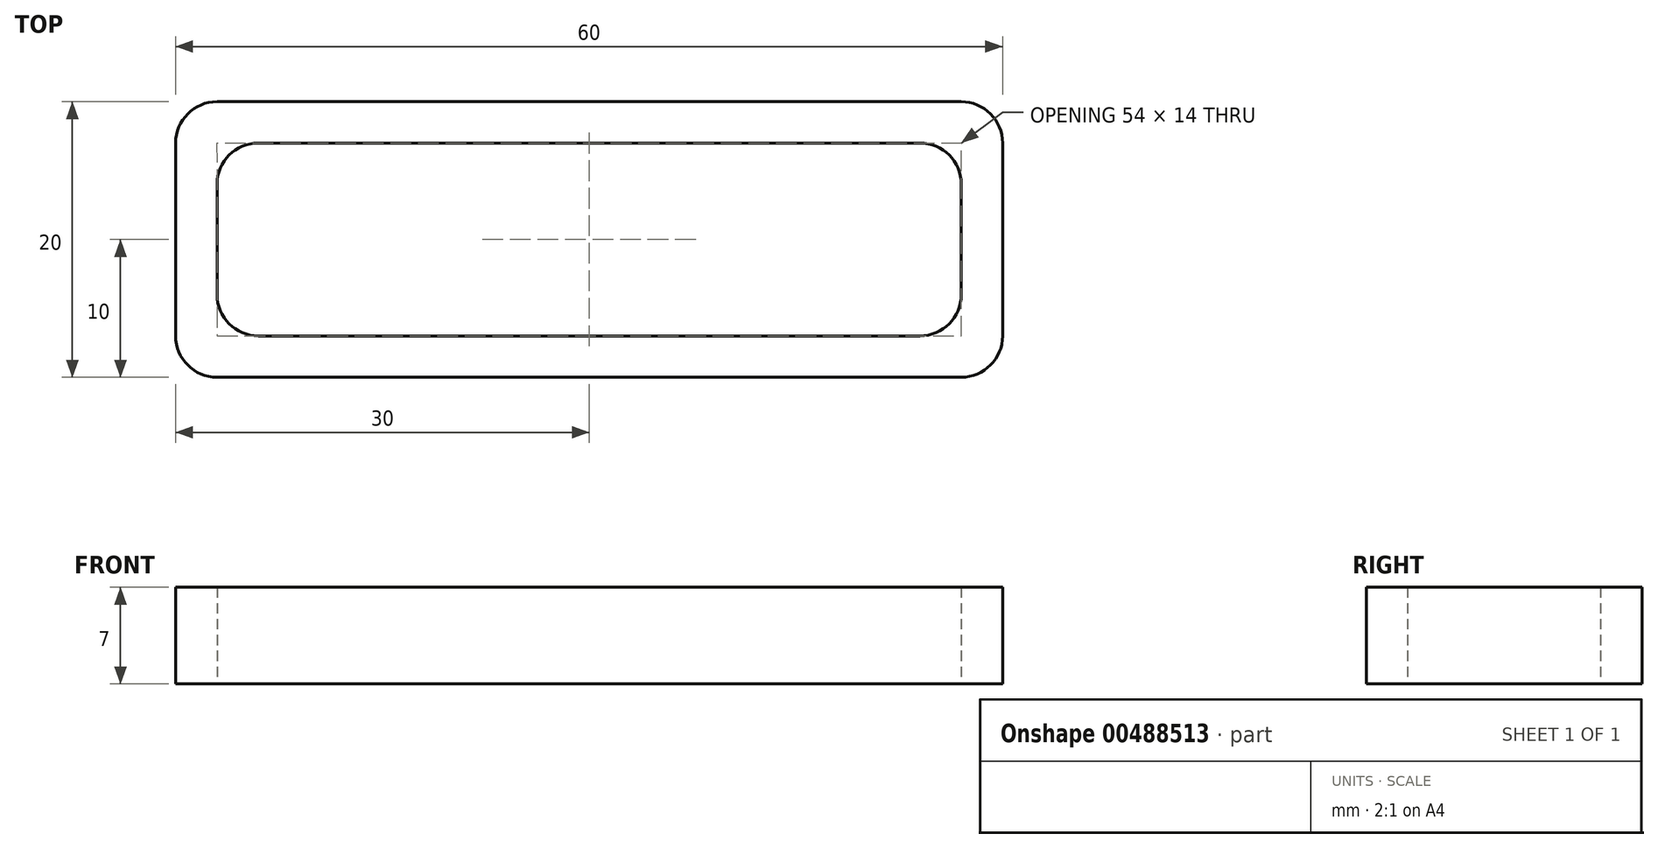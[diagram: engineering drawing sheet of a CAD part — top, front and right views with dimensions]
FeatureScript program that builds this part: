
annotation { "Feature Type Name" : "Feature", "Feature Type Description" : "" }
export const myFeature = defineFeature(function(context is Context, id is Id, definition is map)
    precondition{}
    {
        {
            var Q0;
            Q0=qCreatedBy(makeId("Top.planeOp"),FACE);
            var sketch = newSketch(context, id + "F0", { "sketchPlane" : qUnion([Q0])});
            skLineSegment(sketch, "E0.bottom", {"start": v(30, -10) * mm, "end": v(-30, -10) * mm});
            skLineSegment(sketch, "E0.top", {"start": v(30, 10) * mm, "end": v(-30, 10) * mm});
            skLineSegment(sketch, "E0.left", {"start": v(30, -10) * mm, "end": v(30, 10) * mm});
            skLineSegment(sketch, "E0.right", {"start": v(-30, -10) * mm, "end": v(-30, 10) * mm});
            skPoint(sketch, "E0.middle", {"position": v(0, 0) * mm});
            skLineSegment(sketch, "E1.bottom", {"start": v(-27, 7) * mm, "end": v(27, 7) * mm});
            skLineSegment(sketch, "E1.top", {"start": v(-27, -7) * mm, "end": v(27, -7) * mm});
            skLineSegment(sketch, "E1.left", {"start": v(-27, 7) * mm, "end": v(-27, -7) * mm});
            skLineSegment(sketch, "E1.right", {"start": v(27, 7) * mm, "end": v(27, -7) * mm});
            skSolve(sketch);
        }
        {
            var Q0;
            Q0 = qSketchRegion(id + "F0", true);
            extrude(context, id + "F1", {"entities" : qUnion([Q0]), "endBound" : BoundingType.SYMMETRIC, "depth" : 7 * mm});
        }
        {
            var Q0;
            Q0=makeQuery(id+"F1.opExtrude","SWEPT_EDGE",EDGE,{"disambiguationData":[OSD([sQuery(id+"F0.wireOp",EDGE,"E0.bottom"),sQuery(id+"F0.wireOp",EDGE,"E0.right")])]});
            var Q1;
            Q1=makeQuery(id+"F1.opExtrude","SWEPT_EDGE",EDGE,{"disambiguationData":[OSD([sQuery(id+"F0.wireOp",EDGE,"E0.top"),sQuery(id+"F0.wireOp",EDGE,"E0.right")])]});
            var Q2;
            Q2=makeQuery(id+"F1.opExtrude","SWEPT_EDGE",EDGE,{"disambiguationData":[OSD([sQuery(id+"F0.wireOp",EDGE,"E1.bottom"),sQuery(id+"F0.wireOp",EDGE,"E1.left")])]});
            var Q3;
            Q3=makeQuery(id+"F1.opExtrude","SWEPT_EDGE",EDGE,{"disambiguationData":[OSD([sQuery(id+"F0.wireOp",EDGE,"E1.top"),sQuery(id+"F0.wireOp",EDGE,"E1.left")])]});
            var Q4;
            Q4=makeQuery(id+"F1.opExtrude","SWEPT_EDGE",EDGE,{"disambiguationData":[OSD([sQuery(id+"F0.wireOp",EDGE,"E1.bottom"),sQuery(id+"F0.wireOp",EDGE,"E1.right")])]});
            var Q5;
            Q5=makeQuery(id+"F1.opExtrude","SWEPT_EDGE",EDGE,{"disambiguationData":[OSD([sQuery(id+"F0.wireOp",EDGE,"E1.top"),sQuery(id+"F0.wireOp",EDGE,"E1.right")])]});
            var Q6;
            Q6=makeQuery(id+"F1.opExtrude","SWEPT_EDGE",EDGE,{"disambiguationData":[OSD([sQuery(id+"F0.wireOp",EDGE,"E0.top"),sQuery(id+"F0.wireOp",EDGE,"E0.left")])]});
            var Q7;
            Q7=makeQuery(id+"F1.opExtrude","SWEPT_EDGE",EDGE,{"disambiguationData":[OSD([sQuery(id+"F0.wireOp",EDGE,"E0.bottom"),sQuery(id+"F0.wireOp",EDGE,"E0.left")])]});
            fillet(context, id + "F2", {"entities" : qUnion([Q0, Q1, Q2, Q3, Q4, Q5, Q6, Q7]), "radius" : 3 * mm, "tangentPropagation" : true, "allowEdgeOverflow" : false});
        }
    });
